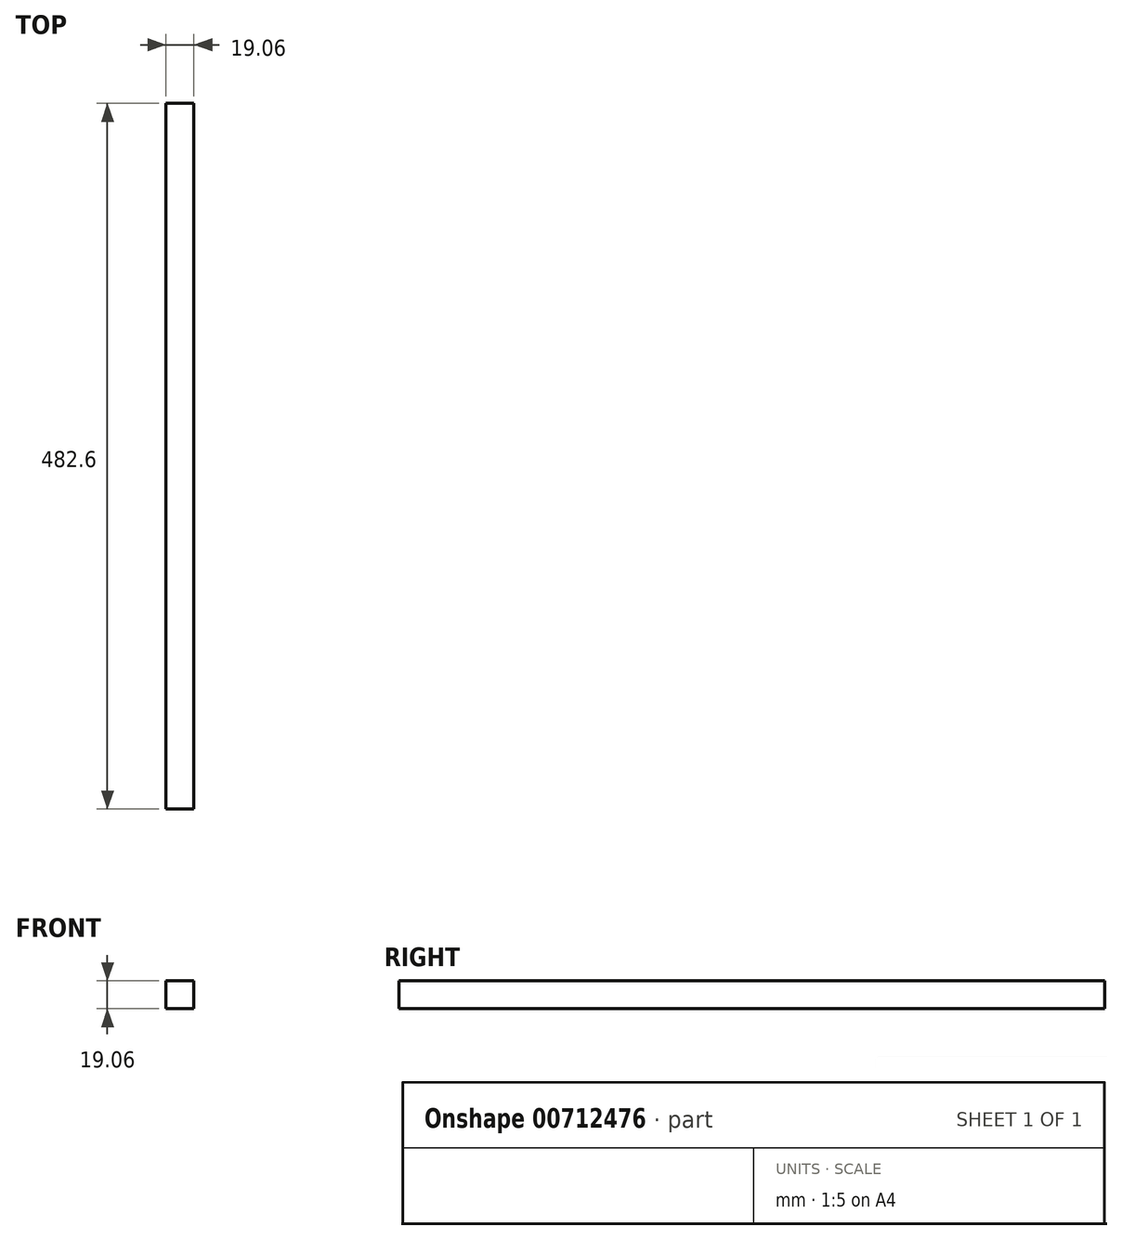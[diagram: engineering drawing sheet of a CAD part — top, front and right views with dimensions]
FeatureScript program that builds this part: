
annotation { "Feature Type Name" : "Feature", "Feature Type Description" : "" }
export const myFeature = defineFeature(function(context is Context, id is Id, definition is map)
    precondition{}
    {
        {
            var Q0;
            Q0=qCreatedBy(makeId("Front.planeOp"),FACE);
            var sketch = newSketch(context, id + "F0", { "sketchPlane" : qUnion([Q0])});
            skLineSegment(sketch, "E0.bottom", {"start": v(-9.52, 9.53) * mm, "end": v(9.53, 9.53) * mm});
            skLineSegment(sketch, "E0.top", {"start": v(-9.53, -9.52) * mm, "end": v(9.52, -9.52) * mm});
            skLineSegment(sketch, "E0.left", {"start": v(-9.52, 9.53) * mm, "end": v(-9.53, -9.52) * mm});
            skLineSegment(sketch, "E0.right", {"start": v(9.53, 9.53) * mm, "end": v(9.52, -9.52) * mm});
            skPoint(sketch, "E0.middle", {"position": v(0, 0) * mm});
            skSolve(sketch);
        }
        {
            var Q0;
            Q0 = qSketchRegion(id + "F0", true);
            extrude(context, id + "F1", {"entities" : qUnion([Q0]), "endBound" : BoundingType.SYMMETRIC, "depth" : 482.6 * mm, "offsetDistance" : 25.4 * mm});
        }
    });
